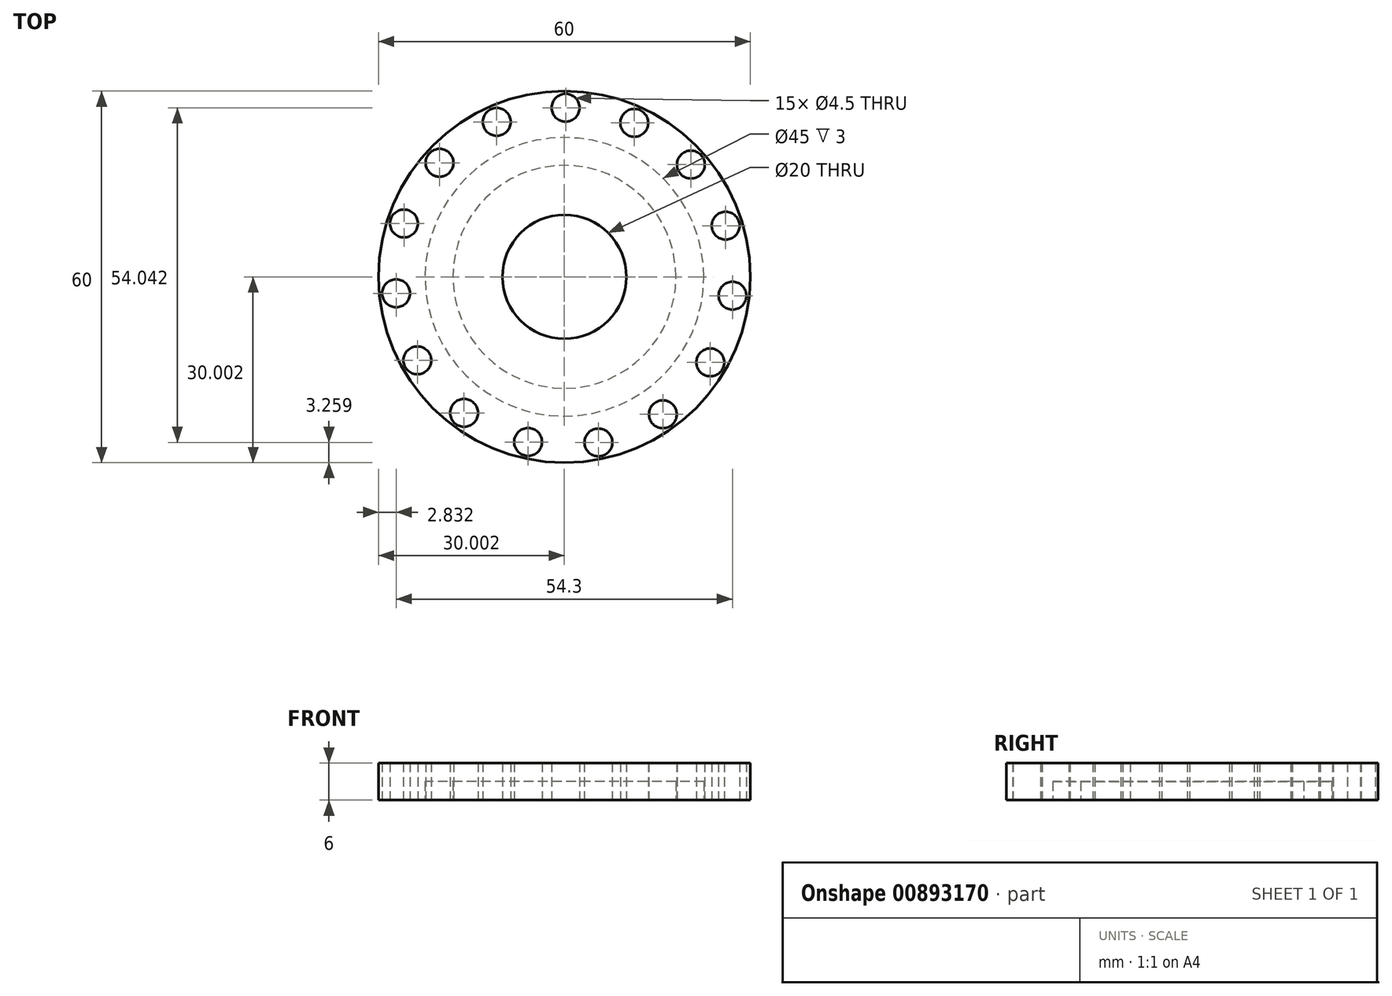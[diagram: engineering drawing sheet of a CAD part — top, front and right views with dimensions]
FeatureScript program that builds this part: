
annotation { "Feature Type Name" : "Feature", "Feature Type Description" : "" }
export const myFeature = defineFeature(function(context is Context, id is Id, definition is map)
    precondition{}
    {
        {
            var Q0;
            Q0=qCreatedBy(makeId("Top.planeOp"),FACE);
            var sketch = newSketch(context, id + "F0", { "sketchPlane" : qUnion([Q0])});
            skCircle(sketch, "E0", {"center": v(-35.53, 25.61) * mm, "radius": 22.5 * mm});
            skCircle(sketch, "E1", {"center": v(-35.53, 25.61) * mm, "radius": 18 * mm});
            skSolve(sketch);
        }
        {
            var Q0;
            Q0=makeQuery(id+"F0.imprint","IMPRINT",FACE,{"disambiguationData":[TD([[makeQuery(id+"F0.imprint","IMPRINT",EDGE,{"derivedFrom":sQuery(id+"F0.wireOp",EDGE,"E0")}),1.0]])]});
            extrude(context, id + "F1", {"entities" : qUnion([Q0]), "depth" : 3 * mm, "offsetDistance" : 25 * mm});
        }
        {
            var Q0;
            Q0=qCreatedBy(makeId("Top.planeOp"),FACE);
            var sketch = newSketch(context, id + "F2", { "sketchPlane" : qUnion([Q0])});
            skCircle(sketch, "E2", {"center": v(-35.53, 25.61) * mm, "radius": 30 * mm});
            skCircle(sketch, "E3", {"center": v(-35.34, 52.91) * mm, "radius": 2.25 * mm});
            skCircle(sketch, "E4.1.0", {"center": v(-46.46, 50.63) * mm, "radius": 2.25 * mm});
            skCircle(sketch, "E4.2.0", {"center": v(-55.69, 44.02) * mm, "radius": 2.25 * mm});
            skCircle(sketch, "E4.3.0", {"center": v(-61.43, 34.23) * mm, "radius": 2.25 * mm});
            skCircle(sketch, "E4.4.0", {"center": v(-62.7, 22.95) * mm, "radius": 2.25 * mm});
            skCircle(sketch, "E4.5.0", {"center": v(-59.27, 12.13) * mm, "radius": 2.25 * mm});
            skCircle(sketch, "E4.6.0", {"center": v(-51.73, 3.64) * mm, "radius": 2.25 * mm});
            skCircle(sketch, "E4.7.0", {"center": v(-41.4, -1.05) * mm, "radius": 2.25 * mm});
            skCircle(sketch, "E4.8.0", {"center": v(-30.04, -1.13) * mm, "radius": 2.25 * mm});
            skCircle(sketch, "E4.9.0", {"center": v(-19.64, 3.41) * mm, "radius": 2.25 * mm});
            skCircle(sketch, "E5.1.10.0", {"center": v(-11.98, 11.8) * mm, "radius": 2.25 * mm});
            skCircle(sketch, "E5.1.11.0", {"center": v(-8.4, 22.57) * mm, "radius": 2.25 * mm});
            skCircle(sketch, "E6.1.12.0", {"center": v(-9.5, 33.86) * mm, "radius": 2.25 * mm});
            skCircle(sketch, "E6.1.13.0", {"center": v(-15.11, 43.74) * mm, "radius": 2.25 * mm});
            skCircle(sketch, "E7.1.14.0", {"center": v(-24.25, 50.47) * mm, "radius": 2.25 * mm});
            skSolve(sketch);
        }
        {
            var Q0;
            Q0=makeQuery(id+"F2.imprint","IMPRINT",FACE,{"disambiguationData":[TD([[makeQuery(id+"F2.imprint","IMPRINT",EDGE,{"derivedFrom":sQuery(id+"F2.wireOp",EDGE,"E2")}),1.0]])]});
            extrude(context, id + "F3", {"entities" : qUnion([Q0]), "depth" : 6 * mm, "offsetDistance" : 25 * mm});
        }
        {
            var Q0;
            Q0 = qSketchRegion(id + "F0", true);
            extrude(context, id + "F4", {"entities" : qUnion([Q0]), "operationType" : NewBodyOperationType.REMOVE, "depth" : 3 * mm, "offsetDistance" : 25 * mm});
        }
        {
            var Q0;
            Q0=makeQuery(id+"F4.boolean.opBoolean","SPLIT",FACE,{"disambiguationData":[TD([makeQuery(id+"F4.opExtrude","SWEPT_FACE",FACE,{"disambiguationData":[OSD([sQuery(id+"F0.wireOp",EDGE,"E1")])]})])],"derivedFrom":makeQuery(id+"F3.opExtrude","CAP_FACE",FACE,{"disambiguationData":[OSD([sQuery(id+"F2.wireOp",EDGE,"E2"),sQuery(id+"F2.wireOp",EDGE,"E3"),sQuery(id+"F2.wireOp",EDGE,"E4.1.0"),sQuery(id+"F2.wireOp",EDGE,"E4.2.0"),sQuery(id+"F2.wireOp",EDGE,"E4.3.0"),sQuery(id+"F2.wireOp",EDGE,"E4.4.0"),sQuery(id+"F2.wireOp",EDGE,"E4.5.0"),sQuery(id+"F2.wireOp",EDGE,"E4.6.0"),sQuery(id+"F2.wireOp",EDGE,"E4.7.0"),sQuery(id+"F2.wireOp",EDGE,"E4.8.0"),sQuery(id+"F2.wireOp",EDGE,"E4.9.0")])],"isStart":true})});
            var sketch = newSketch(context, id + "F5", { "sketchPlane" : qUnion([Q0])});
            skCircle(sketch, "E8", {"center": v(-35.53, -25.61) * mm, "radius": 10 * mm});
            skSolve(sketch);
        }
        {
            var Q0;
            Q0=makeQuery(id+"F5.imprint","IMPRINT",FACE,{"disambiguationData":[TD([[makeQuery(id+"F5.imprint","IMPRINT",EDGE,{"derivedFrom":sQuery(id+"F5.wireOp",EDGE,"E8")}),1.0]])]});
            extrude(context, id + "F6", {"entities" : qUnion([Q0]), "operationType" : NewBodyOperationType.REMOVE, "oppositeDirection" : true, "depth" : 10 * mm, "offsetDistance" : 25 * mm});
        }
    });
